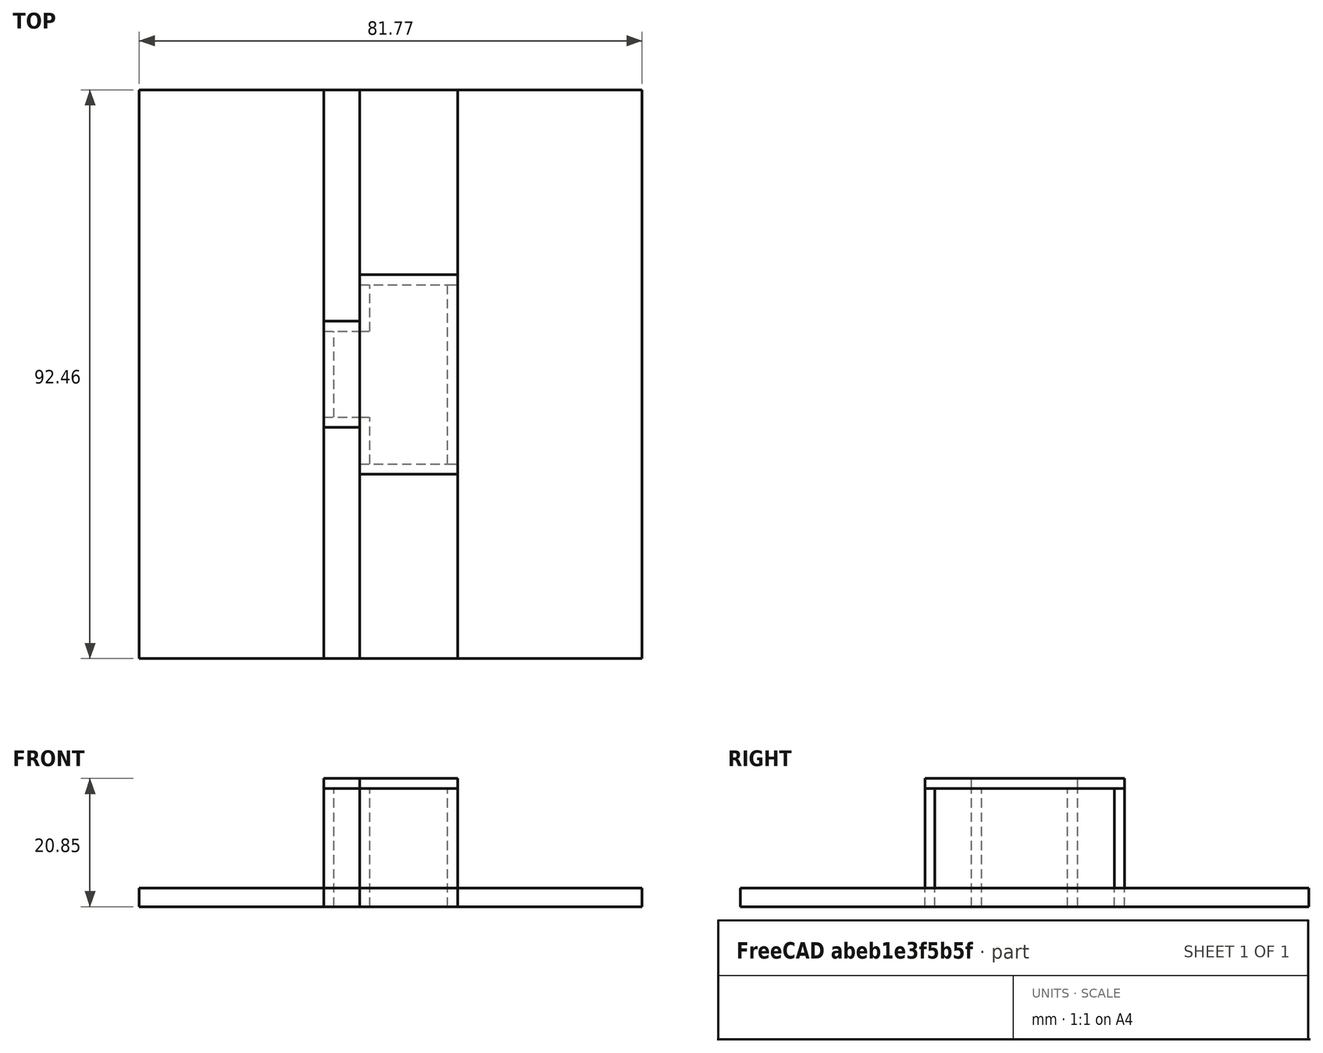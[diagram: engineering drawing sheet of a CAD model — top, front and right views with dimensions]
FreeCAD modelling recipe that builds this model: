
FCSTD DOCUMENT  (FreeCAD 0.21R33694 (Git))
Label: port2
License: All rights reserved
LicenseURL: http://en.wikipedia.org/wiki/All_rights_reserved
objects: Part::Box×16
note: 16 computed .brp shape members not serialized (recipe doc carries the construction recipe); baked Part::Feature solids carry a one-line shape summary decoded from their .brp

FEATURE [Part::Box] Box  label="Bottom"
  AttacherType = Attacher::AttachEngine3D
  Height = 19.2
  Length = 1.65
  Placement = pos=(-1.65,-14.58,0) rot=(0,0,1;0rad)
  Width = 29.16
FEATURE [Part::Box] Box001  label="Left1"
  AttacherType = Attacher::AttachEngine3D
  Height = 19.2
  Length = 15.91
  Placement = pos=(-15.91,14.58,0) rot=(0,0,1;0rad)
  Width = 1.65
FEATURE [Part::Box] Box002  label="Right1"
  AttacherType = Attacher::AttachEngine3D
  Height = 19.2
  Length = 15.91
  Placement = pos=(-15.91,-16.23,0) rot=(0,0,1;0rad)
  Width = 1.65
FEATURE [Part::Box] Box003  label="Left2"
  AttacherType = Attacher::AttachEngine3D
  Height = 19.2
  Length = 1.65
  Placement = pos=(-15.91,6.99,0) rot=(0,0,1;0rad)
  Width = 7.59
FEATURE [Part::Box] Box004  label="Right2"
  AttacherType = Attacher::AttachEngine3D
  Height = 19.2
  Length = 1.65
  Placement = pos=(-15.91,-14.58,0) rot=(0,0,1;0rad)
  Width = 7.59
FEATURE [Part::Box] Box005  label="Left3"
  AttacherType = Attacher::AttachEngine3D
  Height = 19.2
  Length = 5.86
  Placement = pos=(-21.77,6.99,0) rot=(0,0,1;0rad)
  Width = 1.65
FEATURE [Part::Box] Box006  label="Right3"
  AttacherType = Attacher::AttachEngine3D
  Height = 19.2
  Length = 5.86
  Placement = pos=(-21.77,-8.64,0) rot=(0,0,1;0rad)
  Width = 1.65
FEATURE [Part::Box] Box007  label="Top"
  AttacherType = Attacher::AttachEngine3D
  Height = 19.2
  Length = 1.65
  Placement = pos=(-21.77,-6.99,0) rot=(0,0,1;0rad)
  Width = 13.98
FEATURE [Part::Box] Box008  label="Back1"
  AttacherType = Attacher::AttachEngine3D
  Height = 1.65
  Length = 15.91
  Placement = pos=(-15.91,-16.23,19.2) rot=(0,0,1;0rad)
  Width = 32.46
FEATURE [Part::Box] Box009  label="Back2"
  AttacherType = Attacher::AttachEngine3D
  Height = 1.65
  Length = 5.86
  Placement = pos=(-21.77,-8.64,19.2) rot=(0,0,1;0rad)
  Width = 17.28
FEATURE [Part::Box] Box011  label="Plate_Bottom"
  AttacherType = Attacher::AttachEngine3D
  Height = 3
  Length = 30
  Placement = pos=(0,-46.23,0) rot=(0,0,1;0rad)
  Width = 92.46
FEATURE [Part::Box] Box012  label="Plate_Top"
  AttacherType = Attacher::AttachEngine3D
  Height = 3
  Length = 30
  Placement = pos=(-51.77,-46.23,0) rot=(0,0,1;0rad)
  Width = 92.46
FEATURE [Part::Box] Box013  label="Plate_Left1"
  AttacherType = Attacher::AttachEngine3D
  Height = 3
  Length = 5.86
  Placement = pos=(-21.77,8.64,0) rot=(0,0,1;0rad)
  Width = 37.59
FEATURE [Part::Box] Box014  label="Plate_Right1"
  AttacherType = Attacher::AttachEngine3D
  Height = 3
  Length = 5.86
  Placement = pos=(-21.77,-46.23,0) rot=(0,0,1;0rad)
  Width = 37.59
FEATURE [Part::Box] Box015  label="Plate_Left2"
  AttacherType = Attacher::AttachEngine3D
  Height = 3
  Length = 15.91
  Placement = pos=(-15.91,16.23,0) rot=(0,0,1;0rad)
  Width = 30
FEATURE [Part::Box] Box016  label="Plate_Right2"
  AttacherType = Attacher::AttachEngine3D
  Height = 3
  Length = 15.91
  Placement = pos=(-15.91,-46.23,0) rot=(0,0,1;0rad)
  Width = 30
